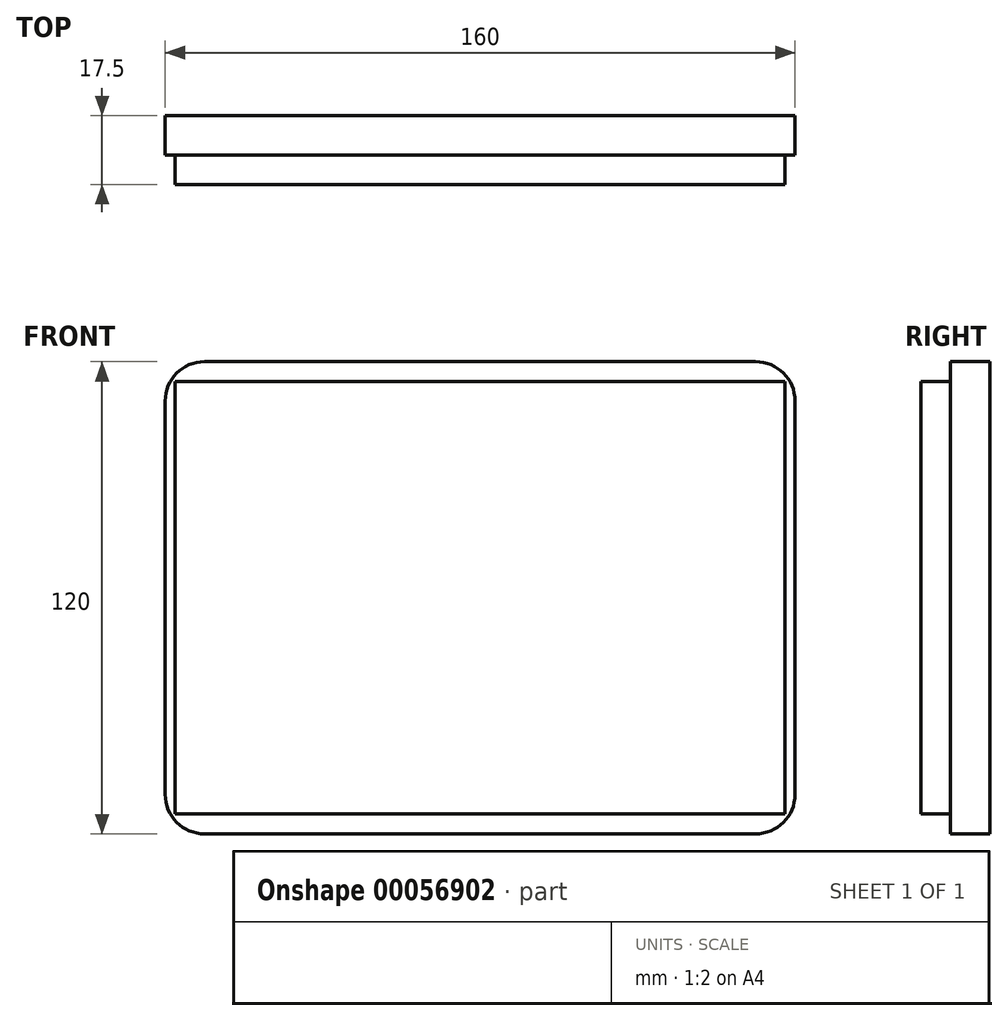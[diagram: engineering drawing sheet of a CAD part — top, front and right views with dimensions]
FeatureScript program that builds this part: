
annotation { "Feature Type Name" : "Feature", "Feature Type Description" : "" }
export const myFeature = defineFeature(function(context is Context, id is Id, definition is map)
    precondition{}
    {
        {
            var Q0;
            Q0=qCreatedBy(makeId("Front.planeOp"),FACE);
            var sketch = newSketch(context, id + "F0", { "sketchPlane" : qUnion([Q0])});
            skLineSegment(sketch, "E0.bottom", {"start": v(-74.97, 71.06) * mm, "end": v(85.03, 71.06) * mm});
            skLineSegment(sketch, "E0.top", {"start": v(-74.97, -48.94) * mm, "end": v(85.03, -48.94) * mm});
            skLineSegment(sketch, "E0.left", {"start": v(-74.97, 71.06) * mm, "end": v(-74.97, -48.94) * mm});
            skLineSegment(sketch, "E0.right", {"start": v(85.03, 71.06) * mm, "end": v(85.03, -48.94) * mm});
            skSolve(sketch);
        }
        {
            var Q0;
            Q0 = qSketchRegion(id + "F0", true);
            extrude(context, id + "F1", {"entities" : qUnion([Q0]), "depth" : 10 * mm});
        }
        {
            var Q0;
            Q0=makeQuery(id+"F1.opExtrude","SWEPT_EDGE",EDGE,{"disambiguationData":[OSD([sQuery(id+"F0.wireOp",EDGE,"E0.bottom"),sQuery(id+"F0.wireOp",EDGE,"E0.left")])]});
            var Q1;
            Q1=makeQuery(id+"F1.opExtrude","SWEPT_EDGE",EDGE,{"disambiguationData":[OSD([sQuery(id+"F0.wireOp",EDGE,"E0.top"),sQuery(id+"F0.wireOp",EDGE,"E0.left")])]});
            var Q2;
            Q2=makeQuery(id+"F1.opExtrude","SWEPT_EDGE",EDGE,{"disambiguationData":[OSD([sQuery(id+"F0.wireOp",EDGE,"E0.bottom"),sQuery(id+"F0.wireOp",EDGE,"E0.right")])]});
            var Q3;
            Q3=makeQuery(id+"F1.opExtrude","SWEPT_EDGE",EDGE,{"disambiguationData":[OSD([sQuery(id+"F0.wireOp",EDGE,"E0.top"),sQuery(id+"F0.wireOp",EDGE,"E0.right")])]});
            fillet(context, id + "F2", {"entities" : qUnion([Q0, Q1, Q2, Q3]), "radius" : 10 * mm, "tangentPropagation" : true, "allowEdgeOverflow" : false});
        }
        {
            var Q0;
            Q0=makeQuery(id+"F1.opExtrude","CAP_FACE",FACE,{"disambiguationData":[OSD([sQuery(id+"F0.wireOp",EDGE,"E0.bottom"),sQuery(id+"F0.wireOp",EDGE,"E0.top"),sQuery(id+"F0.wireOp",EDGE,"E0.left"),sQuery(id+"F0.wireOp",EDGE,"E0.right")])],"isStart":false});
            var sketch = newSketch(context, id + "F3", { "sketchPlane" : qUnion([Q0])});
            skLineSegment(sketch, "E1.bottom", {"start": v(-72.42, 66.01) * mm, "end": v(82.48, 66.01) * mm});
            skLineSegment(sketch, "E1.top", {"start": v(-72.42, -43.89) * mm, "end": v(82.48, -43.89) * mm});
            skLineSegment(sketch, "E1.left", {"start": v(-72.42, 66.01) * mm, "end": v(-72.42, -43.89) * mm});
            skLineSegment(sketch, "E1.right", {"start": v(82.48, 66.01) * mm, "end": v(82.48, -43.89) * mm});
            skSolve(sketch);
        }
        {
            var Q0;
            Q0 = qSketchRegion(id + "F3", true);
            extrude(context, id + "F4", {"entities" : qUnion([Q0]), "operationType" : NewBodyOperationType.ADD, "depth" : 7.5 * mm});
        }
    });
